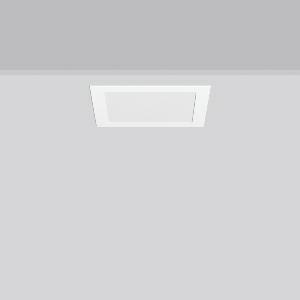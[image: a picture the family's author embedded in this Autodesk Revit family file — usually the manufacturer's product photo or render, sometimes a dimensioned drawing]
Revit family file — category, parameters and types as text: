
# Revit family: toledo_flat_square_e_901487_002_1_76_1fa4
name_source: partatom
category: Lighting Fixtures
units: mm (PartAtom-declared; Revit-internal decimal feet)

## family parameters
Cut with Voids When Loaded = No
Host = Face
Light Source = No
Part Type = Normal
Room Calculation Point = No
Round Connector Dimension = Use Diameter
Shared = No

## types (1)
- TOLEDO FLAT square E (1 x LED Modul 840, 1800 lm, 4000)
    Apparent Load = 17 VA
    CIE Flux Codes = 49 80 96 100 100
    Color Rendering = 80
    Color Temperature = 4000
    Default Elevation = 1800 mm  [stored 5.90551 ft]
    Description = Series: TOLEDO FLAT square
Ultra thin recessed downlight. Housing: die-cast aluminium. Light guide and diffuser made of non-yellowing PMMA, opal matt. Ceiling installation with spring system. Mounting depth depends on ceiling strength. Suitable for through-wiring with separately available accessories. Surface mounted housing as accessory for all sizes. Retrofittable decorative cylinders made of chintz fabric as accessory, optional with satin finish plastic diffuser. Through-wiring box (5 pole) available as accessory. 
Colour: white
Length: 225 mm
Width: 225 mm
Height: 3 mm
Cut-out length: 208 mm
Cut-out width: 208 mm
Recess height: 31-56 mm
Luminaire: recess height: 31-51 mm
Lamp: LED
Socket: without socket
Colour temperature: 4000K
Colour rendering index (CRI): 80
System power: 17 W
Rated luminous flux: 1800 lm
Luminous efficiency: 106 lm/W
Control gear: Converter, dimmable, DALI
Protection class: II
Type of protection: IP 54
    Height = 0 mm  [stored 0 ft]
    Lamp = 1 x LED Modul 840
    Lamp Light Flux = 1800 lm
    Lamp count = 1
    Length = 225 mm
    Lifetime = 50000 h
    Luminous efficacy = 106 lm/W
    Manufacturer = RZB
    ModVariant = No
    Model = 901487.002.1.76
    Mounting Place = Ceiling
    Mounting Type = Recessed
    Number of Poles = 1
    OnlyDefault = Yes
    Power Factor = 1
    Product Name = TOLEDO FLAT square E
    Product group = Recessed downlights
    ProductGroupID = 402
    Protection Class = Protection class II
    Protection Degree = IP 20
    RLX_Detail_Level = 1
    RLX_Emergency_Light_Flux = 0 lm
    RLX_Emergency_Type = 0
    RLX_Emergency_Type_DB = No
    RlxData = <blob elided: 58833 chars, md5=fd01520d>
    Socket = socket
    Standby Power = 0 W
    System Light Flux = 1800 lm
    System Power = 17 W
    Type Comments = Product without accessories
    Type Image = 901487.002.jpg
    URL = http://relux.com
    VarID = ---
    Voltage = 230 V
    Voltage Range = 220-240 V
    Weight = 0.00 kg
    Width = 225 mm

note: [stored X ft] marks values corroborated as IEEE doubles in the binary element streams (Revit-internal decimal feet)

## geometry (parser evidence)
native form markers: Blend x4, Sweep x11
no freeform markers — native parametric forms only
